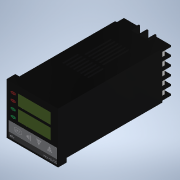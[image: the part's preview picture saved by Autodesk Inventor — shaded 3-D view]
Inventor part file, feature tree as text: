
AUTODESK INVENTOR PART (.ipt)
format: ipt  version: 2020 (Build 240168000, 168)  size: 1,587,200 bytes
history: native  units: in
note: dims shown in document units (in); Inventor stores cm internally (conversion verified against a paired STEP export)
features: sketch x27, extrude x25, projected_geometry x5, emboss x3, chamfer x1, fillet x1, pattern_linear x1
ambient origin geometry x8: Origin, YZ Plane, XZ Plane, XY Plane, X Axis, Y Axis, Z Axis, Center Point
bodies: Solid1 (feature_tree)
feature tree (63):
  extrude  "Extrusion1"  Depth=1.873in
  extrude  "Extrusion2"  Depth=0.04in
  extrude  "Extrusion3"  Depth=1.733in
  extrude  "Extrusion4"  Depth=1.2in
  extrude  "Extrusion5"  Depth=0.28in
  emboss  "Emboss1"
  extrude  "Extrusion6"  Depth=0.4in
  extrude  "Extrusion7"  Depth=0.18in
  sketch  "Sketch9"  dims[d20=0.05in d21=0.25in]
  extrude  "Extrusion8"  Depth=0.08in
  emboss  "Emboss2"
  extrude  "Extrusion9"  Depth=0.25in
  emboss  "Emboss3"
  extrude  "Extrusion10"  Depth=0.0001in TaperAngle=0.0deg
  extrude  "Extrusion11"  Depth=0.0005in
  extrude  "Extrusion12"  Depth=0.0005in
  extrude  "Extrusion13"  Depth=0.3in
  extrude  "Extrusion14"  Depth=0.17in
  extrude  "Extrusion15"  Depth=0.0001in TaperAngle=0.0deg
  extrude  "Extrusion16"  Depth=0.0005in
  extrude  "Extrusion17"  Depth=0.2in
  extrude  "Extrusion18"  Depth=0.025in
  extrude  "Extrusion19"  Depth=0.045in
  chamfer  "Chamfer1"  Distance=0.0002in
  extrude  "Extrusion20"  Depth=0.9875in
  extrude  "Extrusion21"  Depth=0.9875in TaperAngle=0.0deg
  extrude  "Extrusion22"  Depth=0.9875in
  fillet  "Fillet1"  Radius=0.05in
  pattern_linear  "Rectangular Pattern1"  Spacing1=0.05in  [1 undecoded]
  extrude  "Extrusion23"  Depth=0.9875in
  extrude  "Extrusion24"  Depth=0.9875in
  extrude  "Extrusion25"  Depth=0.9875in TaperAngle=0.0deg
  sketch  "Sketch1"  dims[d0=1.883in d1=1.873in]
  sketch  "Sketch2"  dims[d2=0.312in d3=0.0in d4=0.04in]
  sketch  "Sketch3"  dims[d5=0.025in d6=0.0in d7=1.733in]
  sketch  "Sketch4"  dims[d8=3.915in d9=0.0in d10=1.2in]
  sketch  "Sketch5"  dims[d11=0.3in d12=0.28in]
  sketch  "Sketch6"  dims[d13=0.09in d14=0.4in]
  sketch  "Sketch7"  dims[d15=0.0001in d16=0.0in d17=0.18in]
  sketch  "Sketch8"  dims[d18=0.18in d19=0.08in]
  sketch  "Sketch10"  dims[d22=0.25in d23=0.0001in d24=0.0in]
  sketch  "Sketch11"  dims[d25=0.0005in d26=0.0in d27=0.54in]
  sketch  "Sketch12"  dims[d28=0.0005in d29=0.0in d30=0.215in]
  sketch  "Sketch13"  dims[d31=0.0001in d32=0.0in d33=0.3in]
  sketch  "Sketch14"  dims[d34=0.235in d35=0.17in]
  projected_geometry  "Projected Loop1"
  sketch  "Sketch15"  dims[d36=0.01in d37=0.0001in d38=0.0in]
  sketch  "Sketch16"  dims[d39=0.0005in d40=0.0in d41=0.2in]
  sketch  "Sketch17"  dims[d42=0.675in d43=0.2in]
  projected_geometry  "Projected Loop2"
  sketch  "Sketch18"  dims[d44=0.2in d45=0.025in]
  sketch  "Sketch19"  dims[d46=0.015in d47=0.045in]
  sketch  "Sketch20"  dims[d48=0.015in]
  sketch  "Sketch21"  dims[d49=0.015in]
  sketch  "Sketch22"  dims[d50=0.015in]
  sketch  "Sketch23"  dims[d51=0.025in]
  projected_geometry  "Projected Loop3"
  sketch  "Sketch24"  dims[d52=0.015in]
  projected_geometry  "Projected Loop4"
  sketch  "Sketch25"  dims[d53=0.015in]
  sketch  "Sketch26"  dims[d54=0.025in d55=0.0002in d56=0.0in]
  sketch  "Sketch27"  dims[d57=0.0003in d58=0.0in d59=0.325in d60=0.0625in d61=0.0in d62=0.05in d63=0.05in d64=0.05in d65=0.25in d66=0.25in d67=0.0625in d68=0.0in d69=0.5in d70=0.0in d71=0.0625in d72=0.0in d73=0.05in d74=0.05in d75=0.05in d76=0.25in d77=0.25in d78=0.5in d79=0.0in d80=0.5in d81=0.0in d82=0.26in d83=0.05in d84=0.05in d85=0.05in d86=0.05in d87=0.5in d88=0.0in d89=0.5in d90=0.0in d91=0.55in d92=0.55in d93=0.12in d94=0.0in d95=0.236in d96=0.08in d97=0.12in d98=0.0in d99=0.015in d100=0.125in d101=45.0deg d102=0.3in d103=0.24in d104=0.185in d105=0.0in d106=0.21in d107=0.1in d108=0.0in d109=0.05in d110=30.0deg d111=0.05in d112=30.0deg d113=0.025in d114=0.05in d115=0.13in d116=0.025in d117=0.03in d118=0.0in d119=0.025in d120=1.9685in d122=0.307in d123=0.065in d124=0.595in d125=1.6in d126=0.35in d127=0.065in d128=0.065in d129=0.065in d131=0.065in d132=0.065in d133=0.065in d134=0.065in d135=0.25in d136=0.0in d137=0.9875in d138=0.09in d139=0.25in d140=0.0in d141=0.25in d142=0.0in]
  projected_geometry  "Projected Loop5"
note: 1 required parameter value undecoded (feature->parameter linkage not recoverable at this tier; creation-order binding heuristic only, values carry confidence <= 0.55)
